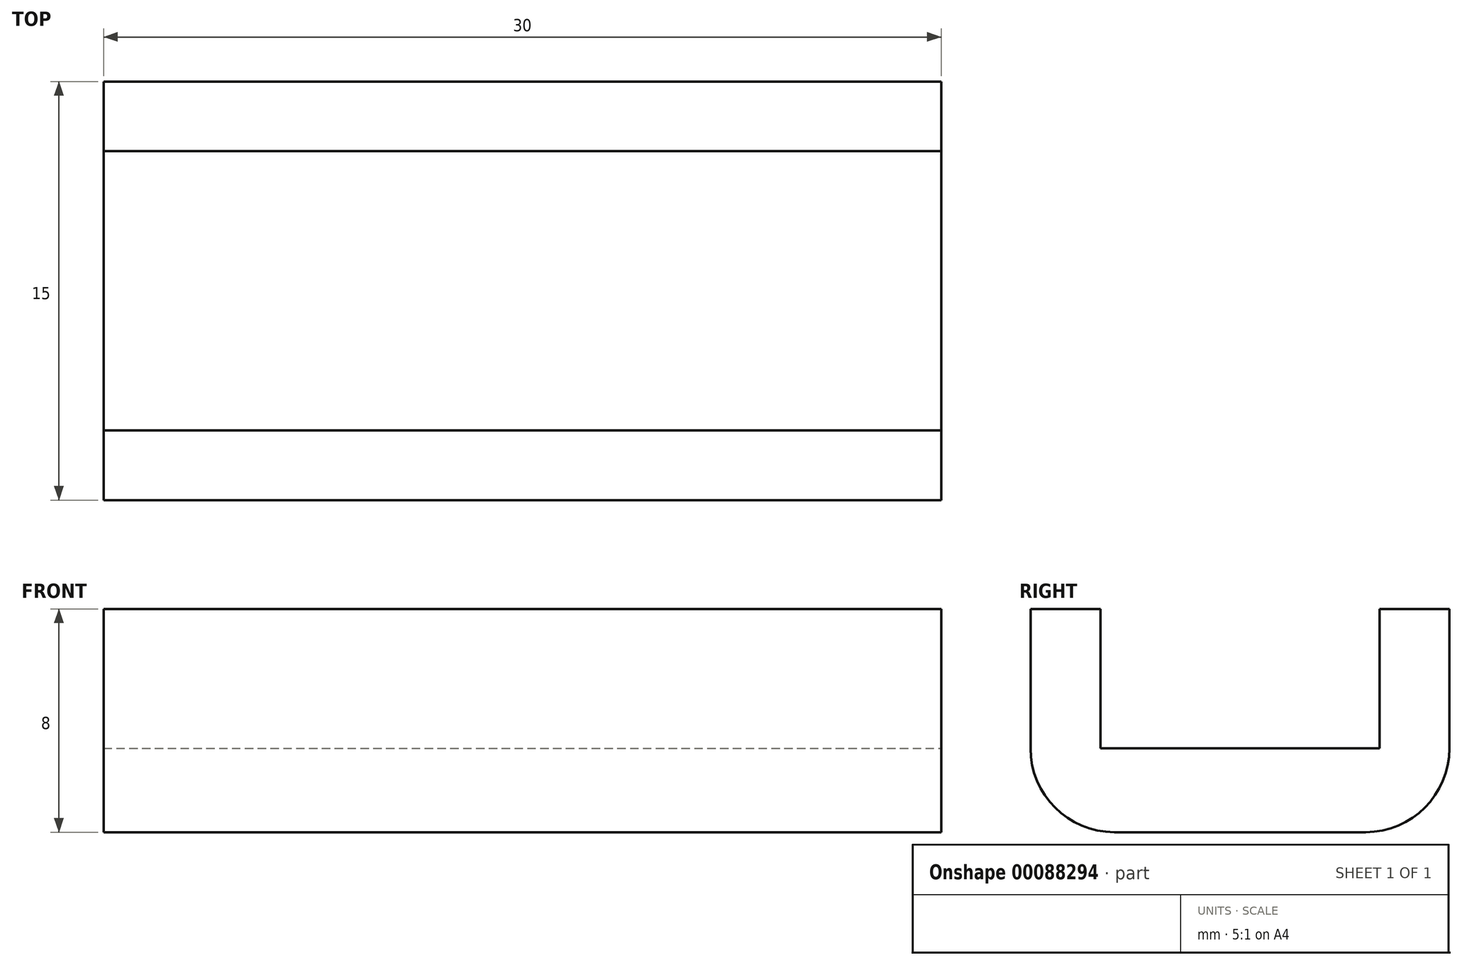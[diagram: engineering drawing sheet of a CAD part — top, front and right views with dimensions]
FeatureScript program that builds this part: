
annotation { "Feature Type Name" : "Feature", "Feature Type Description" : "" }
export const myFeature = defineFeature(function(context is Context, id is Id, definition is map)
    precondition{}
    {
        {
            var Q0;
            Q0=qCreatedBy(makeId("Top.planeOp"),FACE);
            var sketch = newSketch(context, id + "F0", { "sketchPlane" : qUnion([Q0])});
            skLineSegment(sketch, "E0.bottom", {"start": v(-15, 7.5) * mm, "end": v(15, 7.5) * mm});
            skLineSegment(sketch, "E0.top", {"start": v(-15, -7.5) * mm, "end": v(15, -7.5) * mm});
            skLineSegment(sketch, "E0.left", {"start": v(-15, 7.5) * mm, "end": v(-15, -7.5) * mm});
            skLineSegment(sketch, "E0.right", {"start": v(15, 7.5) * mm, "end": v(15, -7.5) * mm});
            skPoint(sketch, "E0.middle", {"position": v(0, 0) * mm});
            skSolve(sketch);
        }
        {
            var Q0;
            Q0=makeQuery(id+"F0.imprint","IMPRINT",FACE,{"disambiguationData":[TD([[makeQuery(id+"F0.imprint","IMPRINT",EDGE,{"derivedFrom":sQuery(id+"F0.wireOp",EDGE,"E0.bottom")}),-1.0]])]});
            extrude(context, id + "F1", {"entities" : qUnion([Q0]), "depth" : 3 * mm});
        }
        {
            var Q0;
            Q0=makeQuery(id+"F1.opExtrude","CAP_FACE",FACE,{"disambiguationData":[OSD([sQuery(id+"F0.wireOp",EDGE,"E0.bottom"),sQuery(id+"F0.wireOp",EDGE,"E0.top"),sQuery(id+"F0.wireOp",EDGE,"E0.left"),sQuery(id+"F0.wireOp",EDGE,"E0.right")])],"isStart":false});
            var sketch = newSketch(context, id + "F2", { "sketchPlane" : qUnion([Q0])});
            skLineSegment(sketch, "E1.0", {"start": v(-15, 5) * mm, "end": v(15, 5) * mm});
            skLineSegment(sketch, "E2.0", {"start": v(-15, -5) * mm, "end": v(15, -5) * mm});
            skLineSegment(sketch, "E3", {"start": v(-15, 5) * mm, "end": v(-15, 7.5) * mm});
            skLineSegment(sketch, "E4", {"start": v(-15, 7.5) * mm, "end": v(15, 7.5) * mm});
            skLineSegment(sketch, "E5", {"start": v(15, 7.5) * mm, "end": v(15, 5) * mm});
            skLineSegment(sketch, "E6", {"start": v(15, -5) * mm, "end": v(15, -7.5) * mm});
            skLineSegment(sketch, "E7", {"start": v(15, -7.5) * mm, "end": v(-15, -7.5) * mm});
            skLineSegment(sketch, "E8", {"start": v(-15, -7.5) * mm, "end": v(-15, -5) * mm});
            skSolve(sketch);
        }
        {
            var Q0;
            Q0=makeQuery(id+"F2.imprint","IMPRINT",FACE,{"disambiguationData":[TD([[makeQuery(id+"F2.imprint","IMPRINT",EDGE,{"derivedFrom":sQuery(id+"F2.wireOp",EDGE,"E1.0")}),1.0]])]});
            var Q1;
            Q1=makeQuery(id+"F2.imprint","IMPRINT",FACE,{"disambiguationData":[TD([[makeQuery(id+"F2.imprint","IMPRINT",EDGE,{"derivedFrom":sQuery(id+"F2.wireOp",EDGE,"E2.0")}),-1.0]])]});
            var Q2;
            Q2 = qConstructionFilter(qBodyType(qCreatedBy(id + "F2" ,EDGE), BodyType.WIRE), ConstructionObject.NO);
            extrude(context, id + "F3", {"entities" : qUnion([Q0, Q1]), "operationType" : NewBodyOperationType.ADD, "surfaceEntities" : qUnion([Q2]), "depth" : 5 * mm});
        }
        {
            var Q0;
            Q0=makeQuery(id+"F3.opExtrude","CAP_EDGE",EDGE,{"disambiguationData":[OSD([sQuery(id+"F2.wireOp",EDGE,"E1.0")])],"isStart":true});
            var Q1;
            Q1=makeQuery(id+"F3.opExtrude","CAP_EDGE",EDGE,{"disambiguationData":[OSD([sQuery(id+"F2.wireOp",EDGE,"E2.0")])],"isStart":true});
            var Q2;
            Q2=makeQuery(id+"F1.opExtrude","CAP_EDGE",EDGE,{"disambiguationData":[OSD([sQuery(id+"F0.wireOp",EDGE,"E0.bottom")])],"isStart":true});
            var Q3;
            Q3=makeQuery(id+"F1.opExtrude","CAP_EDGE",EDGE,{"disambiguationData":[OSD([sQuery(id+"F0.wireOp",EDGE,"E0.top")])],"isStart":true});
            fillet(context, id + "F4", {"entities" : qUnion([Q0, Q1, Q2, Q3]), "radius" : 3 * mm, "tangentPropagation" : true, "allowEdgeOverflow" : false});
        }
    });
